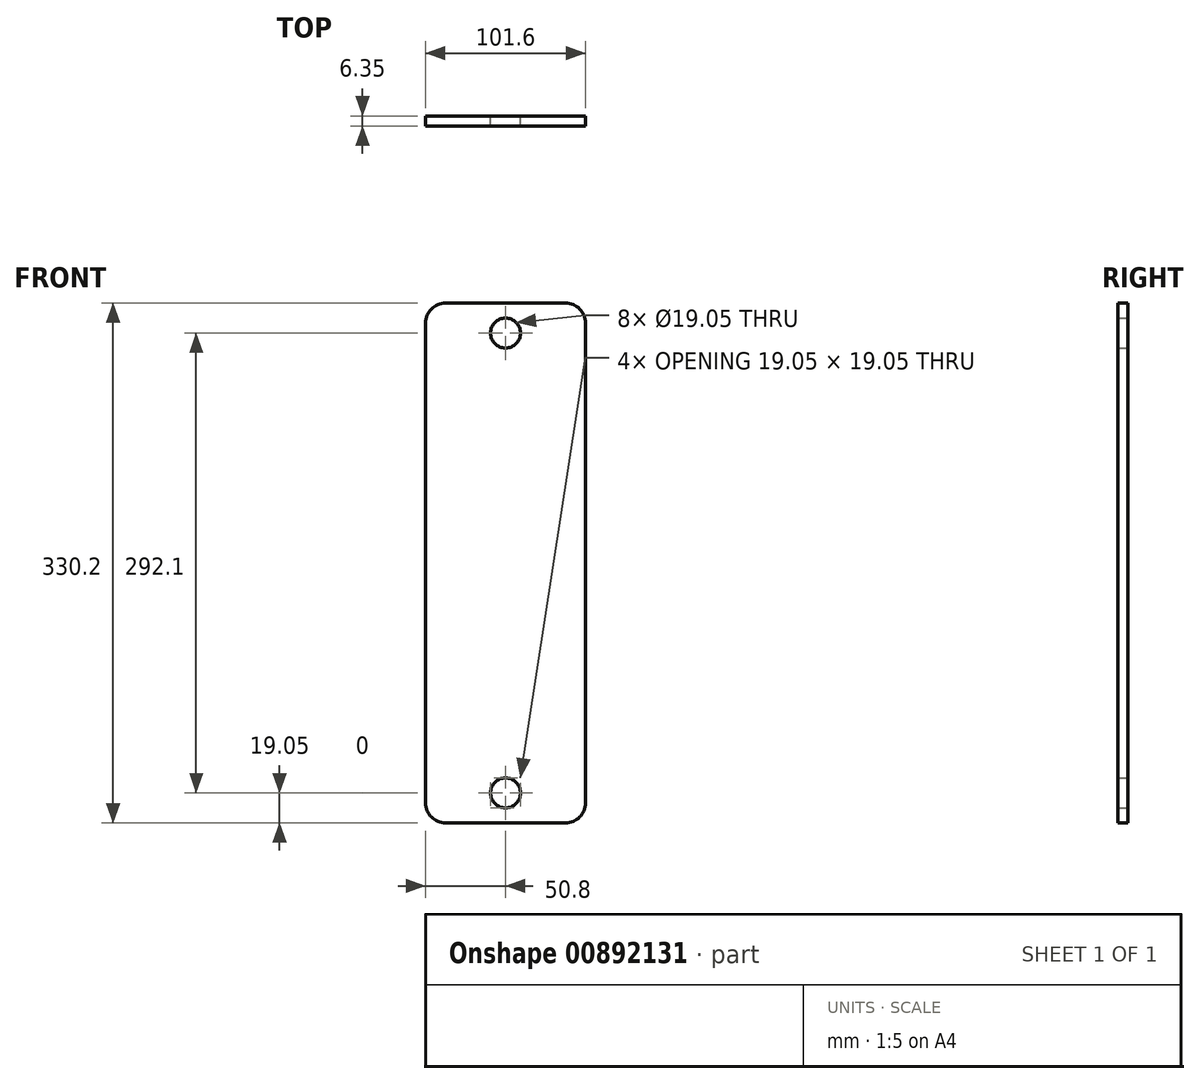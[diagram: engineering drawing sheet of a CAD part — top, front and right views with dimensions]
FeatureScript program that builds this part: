
annotation { "Feature Type Name" : "Feature", "Feature Type Description" : "" }
export const myFeature = defineFeature(function(context is Context, id is Id, definition is map)
    precondition{}
    {
        {
            var Q0;
            Q0=qCreatedBy(makeId("Front.planeOp"),FACE);
            var sketch = newSketch(context, id + "F0", { "sketchPlane" : qUnion([Q0])});
            skLineSegment(sketch, "E0.bottom", {"start": v(-50.8, 165.1) * mm, "end": v(50.8, 165.1) * mm});
            skLineSegment(sketch, "E0.top", {"start": v(-50.8, -165.1) * mm, "end": v(50.8, -165.1) * mm});
            skLineSegment(sketch, "E0.left", {"start": v(-50.8, 165.1) * mm, "end": v(-50.8, -165.1) * mm});
            skLineSegment(sketch, "E0.right", {"start": v(50.8, 165.1) * mm, "end": v(50.8, -165.1) * mm});
            skSolve(sketch);
        }
        {
            var Q0;
            Q0 = qSketchRegion(id + "F0", true);
            extrude(context, id + "F1", {"entities" : qUnion([Q0]), "depth" : 6.35 * mm, "offsetDistance" : 25.4 * mm});
        }
        {
            var Q0;
            Q0=makeQuery(id+"F1.opExtrude","SWEPT_EDGE",EDGE,{"disambiguationData":[OSD([sQuery(id+"F0.wireOp",EDGE,"E0.bottom"),sQuery(id+"F0.wireOp",EDGE,"E0.right")])]});
            var Q1;
            Q1=makeQuery(id+"F1.opExtrude","SWEPT_EDGE",EDGE,{"disambiguationData":[OSD([sQuery(id+"F0.wireOp",EDGE,"E0.bottom"),sQuery(id+"F0.wireOp",EDGE,"E0.left")])]});
            var Q2;
            Q2=makeQuery(id+"F1.opExtrude","SWEPT_EDGE",EDGE,{"disambiguationData":[OSD([sQuery(id+"F0.wireOp",EDGE,"E0.top"),sQuery(id+"F0.wireOp",EDGE,"E0.right")])]});
            var Q3;
            Q3=makeQuery(id+"F1.opExtrude","SWEPT_EDGE",EDGE,{"disambiguationData":[OSD([sQuery(id+"F0.wireOp",EDGE,"E0.top"),sQuery(id+"F0.wireOp",EDGE,"E0.left")])]});
            fillet(context, id + "F2", {"entities" : qUnion([Q0, Q1, Q2, Q3]), "radius" : 12.7 * mm, "tangentPropagation" : true, "allowEdgeOverflow" : false});
        }
        {
            var Q0;
            Q0=qCreatedBy(makeId("Front.planeOp"),FACE);
            var sketch = newSketch(context, id + "F3", { "sketchPlane" : qUnion([Q0])});
            skCircle(sketch, "E1", {"center": v(0, 146.05) * mm, "radius": 9.53 * mm});
            skCircle(sketch, "E2.MirrorC", {"center": v(0, -146.05) * mm, "radius": 9.53 * mm});
            skSolve(sketch);
        }
        {
            var Q0;
            Q0=sQuery(id+"F3.wireOp",VERTEX,"E1.center");
            var Q1;
            Q1=sQuery(id+"F3.wireOp",VERTEX,"E2.MirrorC.center");
            var Q2;
            Q2=makeQuery(id+"F1.opExtrude","SWEPT_BODY",BODY,{"disambiguationData":[OSD([sQuery(id+"F0.wireOp",EDGE,"E0.bottom"),sQuery(id+"F0.wireOp",EDGE,"E0.top"),sQuery(id+"F0.wireOp",EDGE,"E0.left"),sQuery(id+"F0.wireOp",EDGE,"E0.right")])]});
            hole(context, id + "F4", {"style" : HoleStyle.SIMPLE, "endStyle" : HoleEndStyle.THROUGH, "oppositeDirection" : true, "holeDiameter" : 19.05 * mm, "majorDiameter" : 6.35 * mm, "isTappedThrough" : true, "tappedDepth" : 12.7 * mm, "tapClearance" : 3, "locations" : qUnion([Q0, Q1]), "scope" : qUnion([Q2])});
        }
    });
